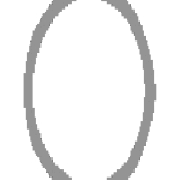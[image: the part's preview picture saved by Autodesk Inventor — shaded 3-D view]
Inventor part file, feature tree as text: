
AUTODESK INVENTOR PART (.ipt)
format: ipt  version: 2021 (Build 250183000, 183)  size: 109,056 bytes
history: native  units: in
note: dims shown in document units (in); Inventor stores cm internally (conversion verified against a paired STEP export)
features: other x4, sketch x3, plane x1
ambient origin geometry x8: Origin, YZ Plane, XZ Plane, XY Plane, X Axis, Y Axis, Z Axis, Center Point
bodies: Solid1 (feature_tree), Body (feature_tree)
feature tree (8):
  other  "Driven Length"
  other  "Frame Generator"
  other  "Start Plane"
  other  "End Plane"
  sketch  "Sketch"  dims[d2=28.9in d4=-0.0in d5=28.9in d6=0.12in d7=0.0in d8=90.0deg d9=28.9in]
  sketch  "Sketch2"  dims[d0=1.0in]
  plane  "Work Plane3"
  sketch  "Sketch3"  dims[d1=0.065in]
